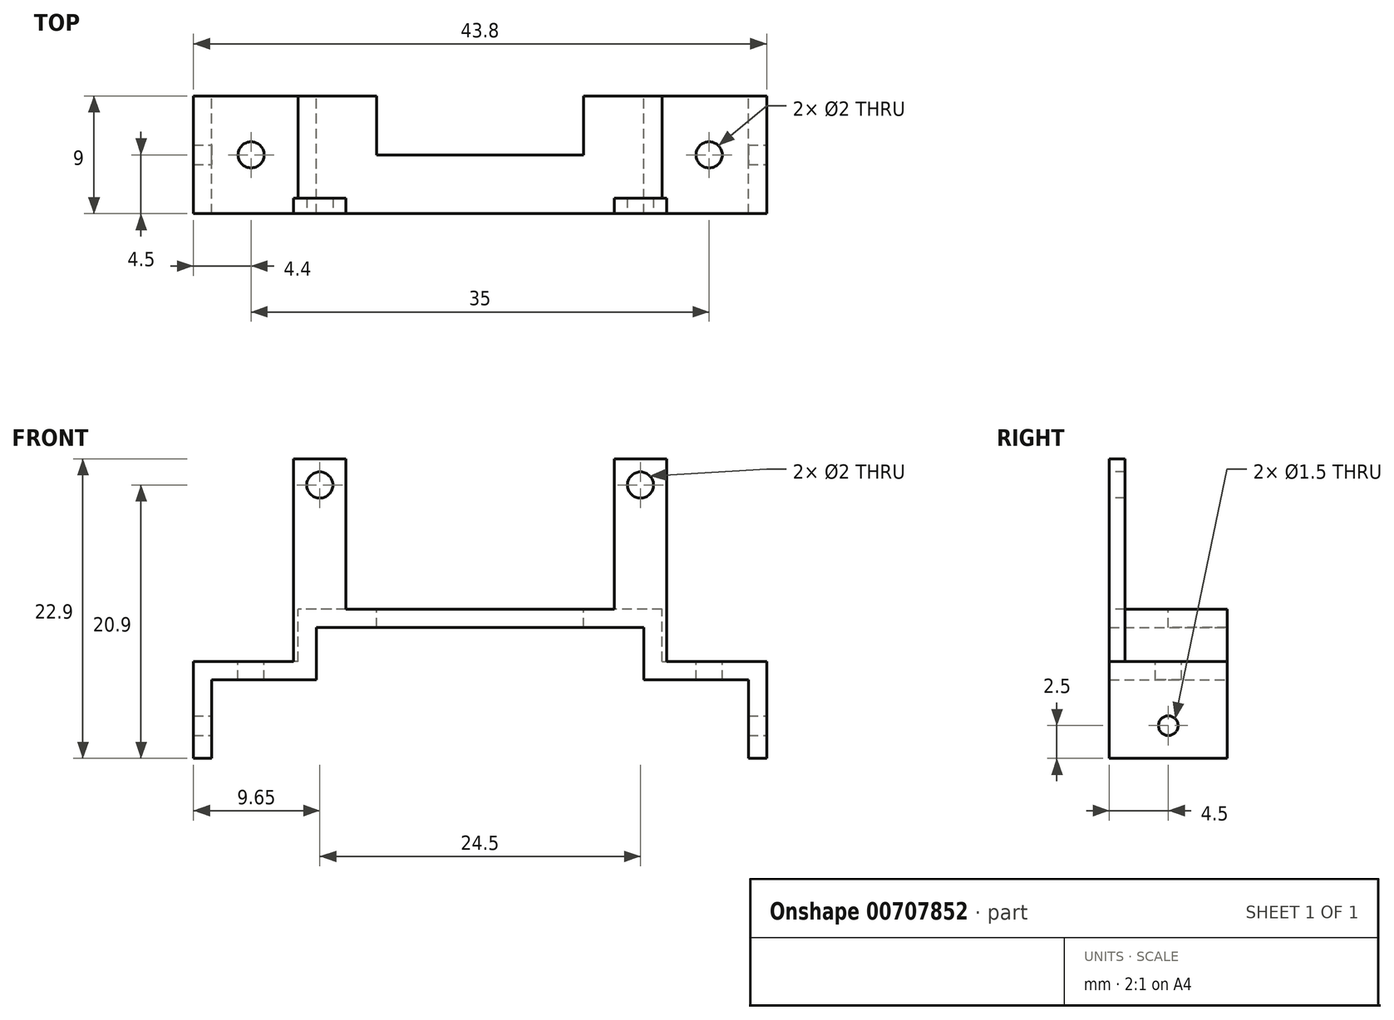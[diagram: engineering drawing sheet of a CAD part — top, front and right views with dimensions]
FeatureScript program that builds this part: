
annotation { "Feature Type Name" : "Feature", "Feature Type Description" : "" }
export const myFeature = defineFeature(function(context is Context, id is Id, definition is map)
    precondition{}
    {
        {
            var Q0;
            Q0=qCreatedBy(makeId("Front.planeOp"),FACE);
            var sketch = newSketch(context, id + "F0", { "sketchPlane" : qUnion([Q0])});
            skLineSegment(sketch, "E0", {"start": v(12.5, 0) * mm, "end": v(20.5, 0) * mm});
            skLineSegment(sketch, "E1", {"start": v(20.5, 0) * mm, "end": v(20.5, -6) * mm});
            skLineSegment(sketch, "E2", {"start": v(20.5, -6) * mm, "end": v(21.9, -6) * mm});
            skLineSegment(sketch, "E3", {"start": v(12.5, 0) * mm, "end": v(12.5, 4) * mm});
            skLineSegment(sketch, "E4", {"start": v(12.5, 4) * mm, "end": v(-12.5, 4) * mm});
            skLineSegment(sketch, "E5.MirrorCS", {"start": v(-12.5, 0) * mm, "end": v(-20.5, 0) * mm});
            skLineSegment(sketch, "E6.MirrorCS", {"start": v(-20.5, 0) * mm, "end": v(-20.5, -6) * mm});
            skLineSegment(sketch, "E7.MirrorCS", {"start": v(-12.5, 0) * mm, "end": v(-12.5, 4) * mm});
            skLineSegment(sketch, "E8.MirrorCS", {"start": v(-20.5, -6) * mm, "end": v(-21.9, -6) * mm});
            skLineSegment(sketch, "E9.1", {"start": v(21.9, 1.4) * mm, "end": v(21.9, -6) * mm});
            skLineSegment(sketch, "E9.2", {"start": v(13.9, 1.4) * mm, "end": v(21.9, 1.4) * mm});
            skLineSegment(sketch, "E9.3", {"start": v(13.9, 1.4) * mm, "end": v(13.9, 5.4) * mm});
            skLineSegment(sketch, "E9.4", {"start": v(13.9, 5.4) * mm, "end": v(-13.9, 5.4) * mm});
            skLineSegment(sketch, "E9.6", {"start": v(-21.9, 1.4) * mm, "end": v(-21.9, -6) * mm});
            skLineSegment(sketch, "E9.7", {"start": v(-13.9, 1.4) * mm, "end": v(-21.9, 1.4) * mm});
            skLineSegment(sketch, "E9.8", {"start": v(-13.9, 1.4) * mm, "end": v(-13.9, 5.4) * mm});
            skLineSegment(sketch, "E10", {"start": v(-21.9, -3.5) * mm, "end": v(21.9, -3.5) * mm, "construction": true});
            skSolve(sketch);
        }
        {
            var Q0;
            Q0 = qSketchRegion(id + "F0", true);
            extrude(context, id + "F1", {"entities" : qUnion([Q0]), "endBound" : BoundingType.SYMMETRIC, "depth" : 9 * mm, "offsetDistance" : 25 * mm});
        }
        {
            var Q0;
            Q0=makeQuery(id+"F1.opExtrude","SWEPT_FACE",FACE,{"disambiguationData":[OSD([sQuery(id+"F0.wireOp",EDGE,"E9.1")])]});
            var sketch = newSketch(context, id + "F2", { "sketchPlane" : qUnion([Q0])});
            skCircle(sketch, "E11", {"center": v(0, -3.5) * mm, "radius": 0.75 * mm});
            skSolve(sketch);
        }
        {
            var Q0;
            Q0 = qSketchRegion(id + "F2", true);
            extrude(context, id + "F3", {"entities" : qUnion([Q0]), "operationType" : NewBodyOperationType.REMOVE, "endBound" : BoundingType.THROUGH_ALL, "oppositeDirection" : true, "depth" : 25 * mm, "offsetDistance" : 25 * mm});
        }
        {
            var Q0;
            Q0=makeQuery(id+"F1.opExtrude","CAP_FACE",FACE,{"disambiguationData":[OSD([sQuery(id+"F0.wireOp",EDGE,"E0"),sQuery(id+"F0.wireOp",EDGE,"E1"),sQuery(id+"F0.wireOp",EDGE,"E2"),sQuery(id+"F0.wireOp",EDGE,"E3"),sQuery(id+"F0.wireOp",EDGE,"E4"),sQuery(id+"F0.wireOp",EDGE,"E5.MirrorCS"),sQuery(id+"F0.wireOp",EDGE,"E6.MirrorCS"),sQuery(id+"F0.wireOp",EDGE,"E7.MirrorCS"),sQuery(id+"F0.wireOp",EDGE,"E8.MirrorCS"),sQuery(id+"F0.wireOp",EDGE,"E9.1"),sQuery(id+"F0.wireOp",EDGE,"E9.2"),sQuery(id+"F0.wireOp",EDGE,"E9.3"),sQuery(id+"F0.wireOp",EDGE,"E9.4"),sQuery(id+"F0.wireOp",EDGE,"E9.6"),sQuery(id+"F0.wireOp",EDGE,"E9.7"),sQuery(id+"F0.wireOp",EDGE,"E9.8")])],"isStart":false});
            var sketch = newSketch(context, id + "F4", { "sketchPlane" : qUnion([Q0])});
            skCircle(sketch, "E12", {"center": v(12.25, 14.9) * mm, "radius": 1 * mm});
            skLineSegment(sketch, "E13.bottom", {"start": v(10.25, 16.9) * mm, "end": v(14.25, 16.9) * mm});
            skLineSegment(sketch, "E13.left", {"start": v(10.25, 16.9) * mm, "end": v(10.25, 5.4) * mm});
            skLineSegment(sketch, "E13.right", {"start": v(14.25, 16.9) * mm, "end": v(14.25, 1.4) * mm});
            skLineSegment(sketch, "E14", {"start": v(12.25, 16.9) * mm, "end": v(12.25, 14.9) * mm, "construction": true});
            skLineSegment(sketch, "E15.MirrorCS", {"start": v(-12.25, 16.9) * mm, "end": v(-12.25, 14.9) * mm, "construction": true});
            skLineSegment(sketch, "E16.MirrorCS", {"start": v(-14.25, 16.9) * mm, "end": v(-14.25, 1.4) * mm});
            skLineSegment(sketch, "E17.MirrorCS", {"start": v(-10.25, 16.9) * mm, "end": v(-10.25, 5.4) * mm});
            skLineSegment(sketch, "E18.MirrorCS", {"start": v(-10.25, 16.9) * mm, "end": v(-14.25, 16.9) * mm});
            skCircle(sketch, "E19.MirrorC", {"center": v(-12.25, 14.9) * mm, "radius": 1 * mm});
            skLineSegment(sketch, "E20", {"start": v(10.25, 5.4) * mm, "end": v(13.9, 5.4) * mm});
            skLineSegment(sketch, "E21", {"start": v(13.9, 5.4) * mm, "end": v(13.9, 1.4) * mm});
            skLineSegment(sketch, "E22", {"start": v(13.9, 1.4) * mm, "end": v(14.25, 1.4) * mm});
            skLineSegment(sketch, "E23", {"start": v(-10.25, 5.4) * mm, "end": v(-13.9, 5.4) * mm});
            skLineSegment(sketch, "E24", {"start": v(-13.9, 5.4) * mm, "end": v(-13.9, 1.4) * mm});
            skLineSegment(sketch, "E25", {"start": v(-13.9, 1.4) * mm, "end": v(-14.25, 1.4) * mm});
            skSolve(sketch);
        }
        {
            var Q0;
            Q0 = qSketchRegion(id + "F4", true);
            extrude(context, id + "F5", {"entities" : qUnion([Q0]), "operationType" : NewBodyOperationType.ADD, "oppositeDirection" : true, "depth" : 1.2 * mm, "offsetDistance" : 25 * mm});
        }
        {
            var Q0;
            Q0=makeQuery(id+"F1.opExtrude","SWEPT_FACE",FACE,{"disambiguationData":[OSD([sQuery(id+"F0.wireOp",EDGE,"E9.4")])]});
            var sketch = newSketch(context, id + "F6", { "sketchPlane" : qUnion([Q0])});
            skCircle(sketch, "E26", {"center": v(-17.5, 0) * mm, "radius": 1 * mm});
            skCircle(sketch, "E27", {"center": v(17.5, 0) * mm, "radius": 1 * mm});
            skLineSegment(sketch, "E28.bottom", {"start": v(7.9, 0) * mm, "end": v(-7.9, 0) * mm});
            skLineSegment(sketch, "E28.top", {"start": v(7.9, 4.5) * mm, "end": v(-7.9, 4.5) * mm});
            skLineSegment(sketch, "E28.left", {"start": v(7.9, 0) * mm, "end": v(7.9, 4.5) * mm});
            skLineSegment(sketch, "E28.right", {"start": v(-7.9, 0) * mm, "end": v(-7.9, 4.5) * mm});
            skPoint(sketch, "E28.middle", {"position": v(0, 2.25) * mm});
            skSolve(sketch);
        }
        {
            var Q0;
            Q0 = qSketchRegion(id + "F6", true);
            extrude(context, id + "F7", {"entities" : qUnion([Q0]), "operationType" : NewBodyOperationType.REMOVE, "endBound" : BoundingType.THROUGH_ALL, "oppositeDirection" : true, "depth" : 25 * mm, "offsetDistance" : 25 * mm});
        }
    });
